# Revit family: 210_CAD O Integral EI 100 VLG 48
name_source: partatom
category: Mechanical Equipment
units: mm (PartAtom-declared; Revit-internal decimal feet)

## family parameters
Always vertical = Yes
Cut with Voids When Loaded = No
Part Type = Breaks Into
Room Calculation Point = No
Round Connector Dimension = Use Diameter
Shared = No
Work Plane-Based = No

## types (1)
- CAD O Integral EI 100 VLG 48
    AA1 = 1206 mm  [stored 3.95669 ft]
    B = 1100 mm
    BB1 = 868 mm
    BH1 = 590 mm  [stored 1.9357 ft]
    BH2 = 2 mm  [stored 0.00656168 ft]
    BH2__ve = -2 mm  [stored -0.00656168 ft]
    BH3 = 690 mm
    BH4 = 245 mm  [stored 0.803806 ft]
    BH5 = 1135 mm  [stored 3.72375 ft]
    CAT0 = Yes
    H = 610 mm
    HH1 = 1971 mm  [stored 6.46654 ft]
    MM1 = 590 mm  [stored 1.9357 ft]
    MM2 = 1480 mm  [stored 4.85564 ft]
    Manufacturer = VIM
    W = 500 mm
    magiPartTypeId = 210
    magiProductCode = CAD O Integral EI 100 VLG 48
    magiProductFamilyId = CAD O Integral EI 100 VLG 48
    magiProductId = CAD O Integral EI 100 VLG 48

note: [stored X ft] marks values corroborated as IEEE doubles in the binary element streams (Revit-internal decimal feet)

## geometry (parser evidence)
native form markers: Sweep x2
no freeform markers — native parametric forms only
